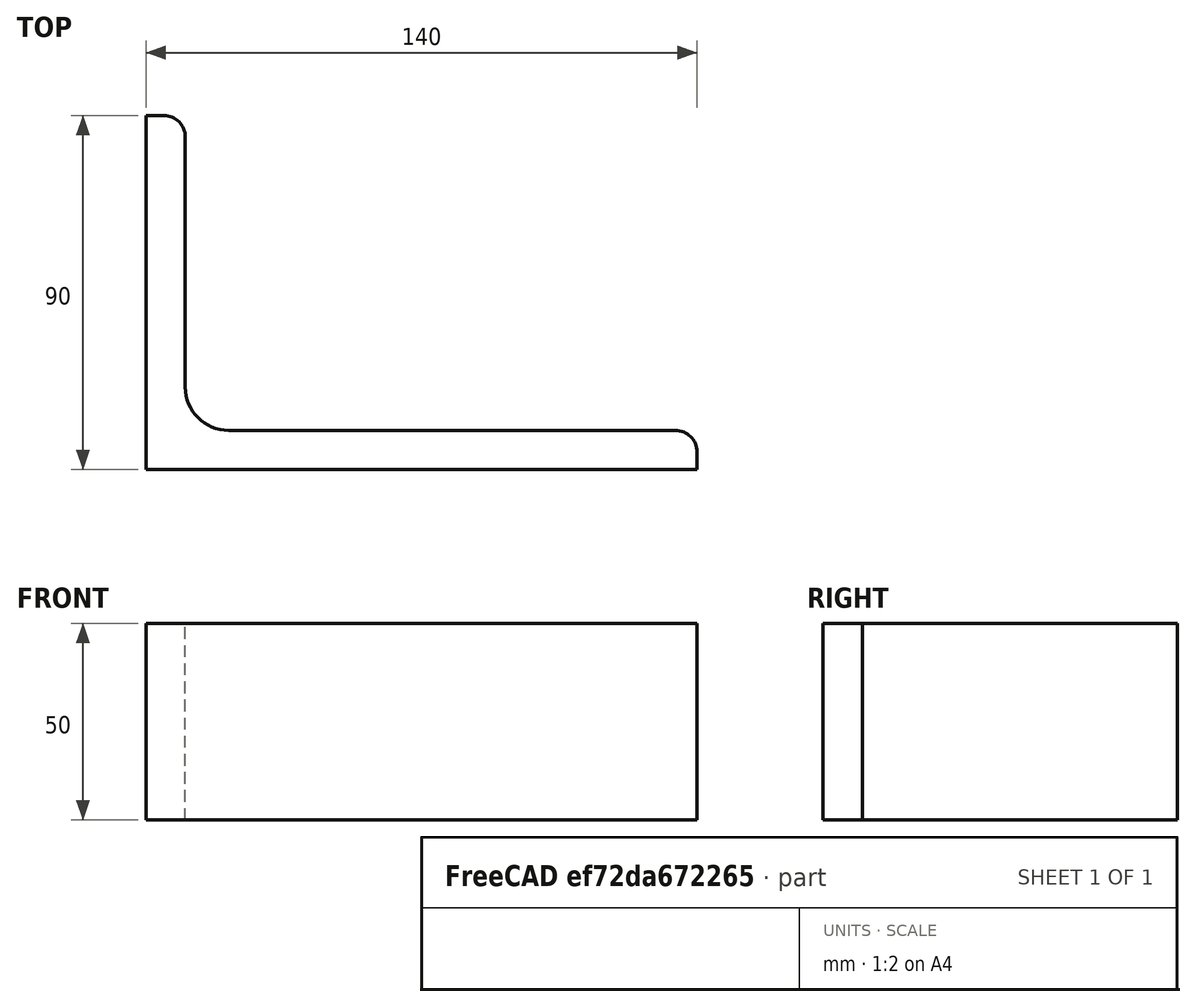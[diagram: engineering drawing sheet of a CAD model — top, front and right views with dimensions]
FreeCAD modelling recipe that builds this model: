
FCSTD DOCUMENT  (FreeCAD 0.15R4671 (Git))
Label: Angle Bar 140x90x10 EN10056 S235JR
License: All rights reserved
LicenseURL: http://en.wikipedia.org/wiki/All_rights_reserved
objects: Sketcher::SketchObject×1, Part::Extrusion×1
note: 2 computed .brp shape members not serialized (recipe doc carries the construction recipe); baked Part::Feature solids carry a one-line shape summary decoded from their .brp

FEATURE [Sketcher::SketchObject] Sketch
  sketch-geometry (9):
    g0: LineSegment StartX=0 StartY=0 StartZ=0 EndX=140 EndY=0 EndZ=0
    g1: LineSegment StartX=140 StartY=0 StartZ=0 EndX=140 EndY=4.5 EndZ=0
    g2: LineSegment StartX=134.5 StartY=10 StartZ=0 EndX=21 EndY=10 EndZ=0
    g3: LineSegment StartX=0 StartY=0 StartZ=0 EndX=0 EndY=90 EndZ=0
    g4: LineSegment StartX=0 StartY=90 StartZ=0 EndX=4.5 EndY=90 EndZ=0
    g5: LineSegment StartX=10 StartY=84.5 StartZ=0 EndX=10 EndY=21 EndZ=0
    g6: ArcOfCircle CenterX=21 CenterY=21 CenterZ=0 NormalX=0 NormalY=0 NormalZ=1 Radius=11 StartAngle=3.14159 EndAngle=4.71239
    g7: ArcOfCircle CenterX=4.5 CenterY=84.5 CenterZ=0 NormalX=0 NormalY=0 NormalZ=1 Radius=5.5 StartAngle=0 EndAngle=1.5708
    g8: ArcOfCircle CenterX=134.5 CenterY=4.5 CenterZ=0 NormalX=0 NormalY=0 NormalZ=1 Radius=5.5 StartAngle=0 EndAngle=1.5708
  constraints (23):
    c: Coincident(g0,g-1)
    c: Horizontal(g0)
    c: Coincident(g1,g0)
    c: Vertical(g1)
    c: Horizontal(g2)
    c: Coincident(g3,g-1)
    c: Vertical(g3)
    c: Coincident(g4,g3)
    c: Horizontal(g4)
    c: Vertical(g5)
    c: Tangent(g5,g6) = -1.5708
    c: Tangent(g2,g6) = 1.5708
    c: Tangent(g4,g7) = 1.5708
    c: Tangent(g5,g7) = 1.5708
    c: Tangent(g2,g8) = -1.5708
    c: Tangent(g1,g8) = -1.5708
    c: DistanceX(g0) = 140
    c: DistanceY(g3) = 90
    c: DistanceY(g0,g2) = 10
    c: DistanceX(g3,g5) = 10
    c: Radius(g6) = 11
    c: Radius(g8) = 5.5
    c: Radius(g7) = 5.5
FEATURE [Part::Extrusion] Extrude  label="Angle Bar 140x90x10 EN10056 S235JR"
  Base = -> Sketch
  Dir = (0,0,50)
  Solid = true
